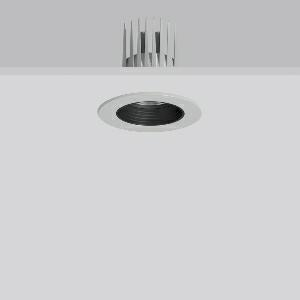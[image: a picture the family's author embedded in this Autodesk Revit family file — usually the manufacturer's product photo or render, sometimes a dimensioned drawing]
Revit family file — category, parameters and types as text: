
# Revit family: heledon_mini_e_901754_004_2_9739
name_source: partatom
category: Lighting Fixtures
units: mm (PartAtom-declared; Revit-internal decimal feet)

## family parameters
Cut with Voids When Loaded = No
Host = Face
Light Source = No
Part Type = Normal
Room Calculation Point = No
Round Connector Dimension = Use Diameter
Shared = No

## types (1)
- HELEDON mini E (1 x LED Modul 927, 3050 lm, 2700)
    Apparent Load = 29 VA
    Approval mark = CE
    CIE Flux Codes = 80 99 100 100 100
    Color Rendering = 92
    Color Temperature = 2700
    Default Elevation = 1800 mm
    Description = Series: HELEDON mini
Round recessed downlight. Housing: die-cast aluminium, powder-coated. Black plastic ring and recessed LED to prevent glare from the side. Optical assembly with lens made of plastic (polycarbonate) for the best homogeneous light distribution - can be changed without tools. Best colour rendering index Ra>90. Suitable for Recessed ceiling mounting. Installation without tools thanks to spring fastening system. Including separate LED converter with connecting cable 600 mm.High quality converter without flickering and stroboscopic effect. Through-wiring box (5 pole) available as accessory. The following accessories can be mounted without use of tools: interchangeable lenses, decorative glasses, honeycomb louvre, clear and frosted diffusers, white interchangeable plastic ring. 
Colour: silver
Diameter: 124 mm
Height: 3 mm
Cut-out diameter: 114 mm
Recess height: 170 mm
Luminaire: recess height: 120 mm
Lamp: LED
Socket: without socket
Colour temperature: 2700K
Colour rendering index (CRI): 92
System power: 29 W
Rated luminous flux: 3050 lm
Luminous efficiency: 105 lm/W
Control gear: Regulated power supply
Protection class: II
Type of protection: IP 20
    Height = 0 mm  [stored 0 ft]
    Lamp = 1 x LED Modul 927
    Lamp Light Flux = 3050 lm
    Lamp count = 1
    Length = 124 mm  [stored 0.406824 ft]
    Lifetime = 50000 h
    Luminous efficacy = 105 lm/W
    Manufacturer = RZB
    ModVariant = No
    Model = 901754.004.2
    Mounting Place = Ceiling
    Mounting Type = Recessed
    Number of Poles = 1
    OnlyDefault = Yes
    Power Factor = 1
    Product Name = HELEDON mini E
    Product group = Recessed downlights
    ProductGroupID = 402
    Protection Class = Protection class II
    Protection Degree = IP 20
    RLX_Detail_Level = 1
    RLX_Emergency_Light_Flux = 0 lm
    RLX_Emergency_Type = 0
    RLX_Emergency_Type_DB = No
    RlxData = <blob elided: 125521 chars, md5=4ac22bd2>
    Socket = socket
    Standby Power = 0 W
    System Light Flux = 3050 lm
    System Power = 29 W
    Type Comments = Product without accessories
    Type Image = 901656.004.jpg
    URL = http://relux.com
    VarID = ---
    Voltage = 230 V
    Voltage Range = 220-240 V
    Weight = 0.00 kg
    Width = 0 mm  [stored 0 ft]

note: [stored X ft] marks values corroborated as IEEE doubles in the binary element streams (Revit-internal decimal feet)

## geometry (parser evidence)
native form markers: Blend x4, Sweep x10
no freeform markers — native parametric forms only
